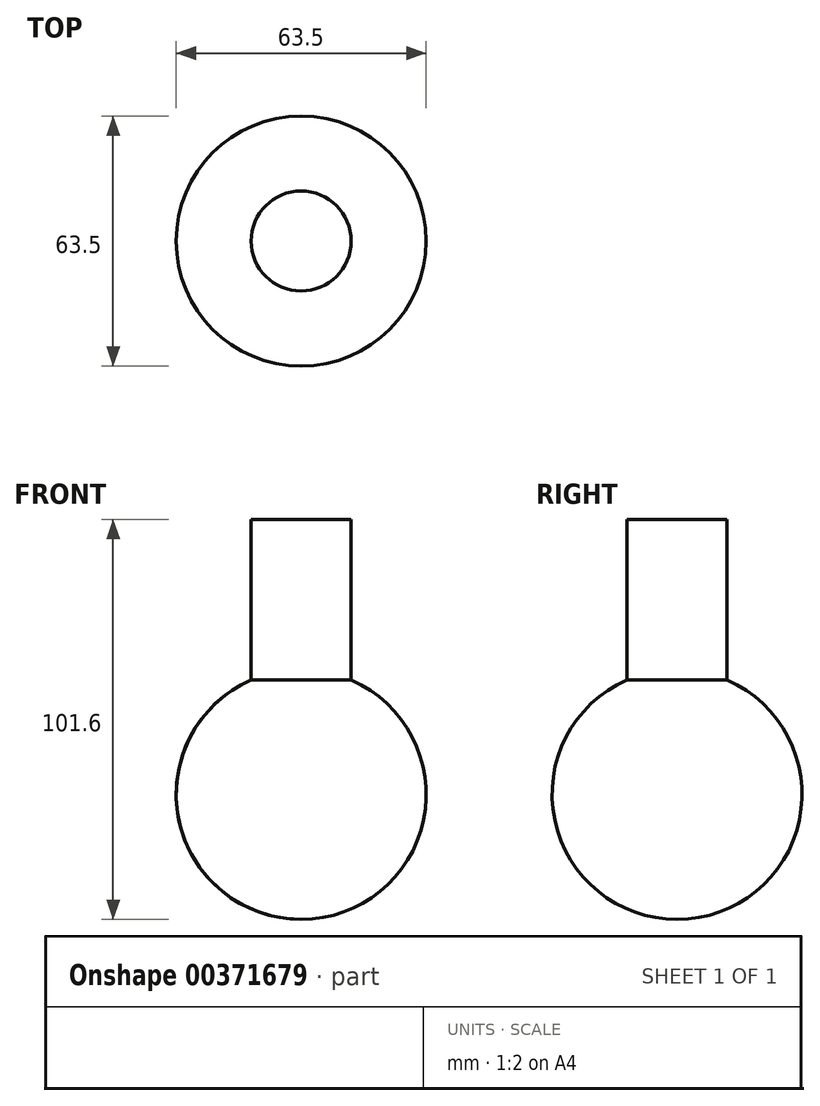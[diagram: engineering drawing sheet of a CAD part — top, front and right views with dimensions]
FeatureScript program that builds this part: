
annotation { "Feature Type Name" : "Feature", "Feature Type Description" : "" }
export const myFeature = defineFeature(function(context is Context, id is Id, definition is map)
    precondition{}
    {
        {
            var Q0;
            Q0=qCreatedBy(makeId("Front.planeOp"),FACE);
            var sketch = newSketch(context, id + "F0", { "sketchPlane" : qUnion([Q0])});
            skArc(sketch, "E0", {"start": v(0, -31.75) * mm, "mid": v(31.08, -6.49) * mm, "end": v(12.7, 29.1) * mm});
            skLineSegment(sketch, "E1", {"start": v(0, 69.85) * mm, "end": v(12.7, 69.85) * mm});
            skLineSegment(sketch, "E2", {"start": v(12.7, 69.85) * mm, "end": v(12.7, 29.1) * mm});
            skPoint(sketch, "E3.start.orphan", {"position": v(0, 31.75) * mm});
            skLineSegment(sketch, "E4", {"start": v(0, -31.75) * mm, "end": v(0, 69.85) * mm});
            skSolve(sketch);
        }
        {
            var Q0;
            Q0=makeQuery(id+"F0.imprint","IMPRINT",FACE,{"disambiguationData":[TD([[makeQuery(id+"F0.imprint","IMPRINT",EDGE,{"derivedFrom":sQuery(id+"F0.wireOp",EDGE,"E0")}),1.0]])]});
            var Q1;
            Q1=sQuery(id+"F0.wireOp",EDGE,"E4");
            revolve(context, id + "F1", {"entities" : qUnion([Q0]), "axis" : qUnion([Q1]), "revolveType" : RevolveType.FULL});
        }
    });
